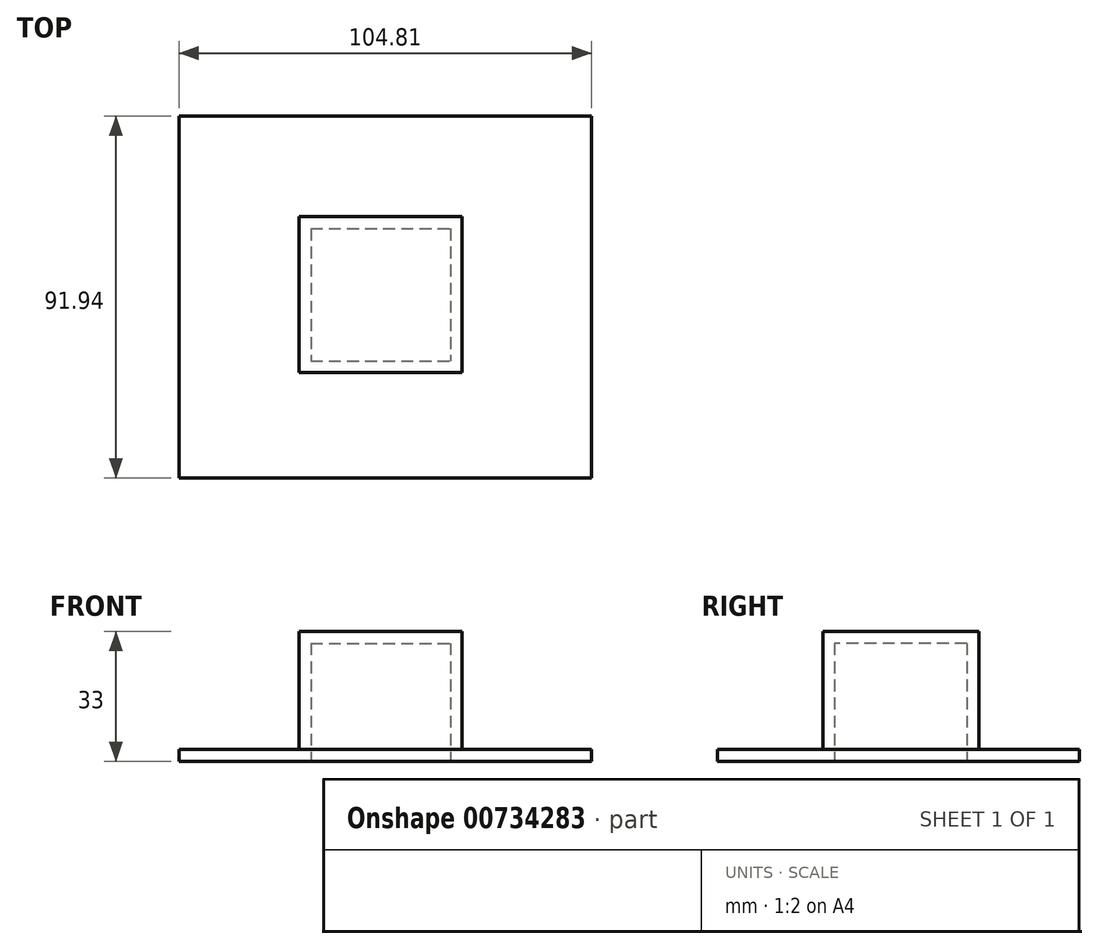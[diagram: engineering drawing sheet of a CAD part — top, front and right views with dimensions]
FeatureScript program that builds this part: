
annotation { "Feature Type Name" : "Feature", "Feature Type Description" : "" }
export const myFeature = defineFeature(function(context is Context, id is Id, definition is map)
    precondition{}
    {
        {
            var Q0;
            Q0=qCreatedBy(makeId("Top.planeOp"),FACE);
            var sketch = newSketch(context, id + "F0", { "sketchPlane" : qUnion([Q0])});
            skLineSegment(sketch, "E0.bottom", {"start": v(-51.82, 43.63) * mm, "end": v(52.99, 43.63) * mm});
            skLineSegment(sketch, "E0.top", {"start": v(-51.82, -48.31) * mm, "end": v(52.99, -48.31) * mm});
            skLineSegment(sketch, "E0.left", {"start": v(-51.82, 43.63) * mm, "end": v(-51.82, -48.31) * mm});
            skLineSegment(sketch, "E0.right", {"start": v(52.99, 43.63) * mm, "end": v(52.99, -48.31) * mm});
            skSolve(sketch);
        }
        {
            var Q0;
            Q0=makeQuery(id+"F0.imprint","IMPRINT",FACE,{"disambiguationData":[TD([[makeQuery(id+"F0.imprint","IMPRINT",EDGE,{"derivedFrom":sQuery(id+"F0.wireOp",EDGE,"E0.bottom")}),-1.0]])]});
            extrude(context, id + "F1", {"entities" : qUnion([Q0]), "depth" : 3 * mm, "offsetDistance" : 25.4 * mm});
        }
        {
            var Q0;
            Q0=makeQuery(id+"F1.opExtrude","CAP_FACE",FACE,{"disambiguationData":[OSD([sQuery(id+"F0.wireOp",EDGE,"E0.bottom"),sQuery(id+"F0.wireOp",EDGE,"E0.top"),sQuery(id+"F0.wireOp",EDGE,"E0.left"),sQuery(id+"F0.wireOp",EDGE,"E0.right")])],"isStart":false});
            var sketch = newSketch(context, id + "F2", { "sketchPlane" : qUnion([Q0])});
            skLineSegment(sketch, "E1.bottom", {"start": v(-21.3, 18.08) * mm, "end": v(20.15, 18.08) * mm});
            skLineSegment(sketch, "E1.top", {"start": v(-21.3, -21.53) * mm, "end": v(20.15, -21.53) * mm});
            skLineSegment(sketch, "E1.left", {"start": v(-21.3, 18.08) * mm, "end": v(-21.3, -21.53) * mm});
            skLineSegment(sketch, "E1.right", {"start": v(20.15, 18.08) * mm, "end": v(20.15, -21.53) * mm});
            skSolve(sketch);
        }
        {
            var Q0;
            Q0=makeQuery(id+"F2.imprint","IMPRINT",FACE,{"disambiguationData":[TD([[makeQuery(id+"F2.imprint","IMPRINT",EDGE,{"derivedFrom":sQuery(id+"F2.wireOp",EDGE,"E1.bottom")}),-1.0]])]});
            extrude(context, id + "F3", {"entities" : qUnion([Q0]), "operationType" : NewBodyOperationType.ADD, "depth" : 30 * mm, "offsetDistance" : 25 * mm});
        }
        {
            var Q0;
            Q0=makeQuery(id+"F1.opExtrude","CAP_FACE",FACE,{"disambiguationData":[OSD([sQuery(id+"F0.wireOp",EDGE,"E0.bottom"),sQuery(id+"F0.wireOp",EDGE,"E0.top"),sQuery(id+"F0.wireOp",EDGE,"E0.left"),sQuery(id+"F0.wireOp",EDGE,"E0.right")])],"isStart":true});
            shell(context, id + "F4", {"entities" : qUnion([Q0]), "thickness" : 3 * mm});
        }
    });
